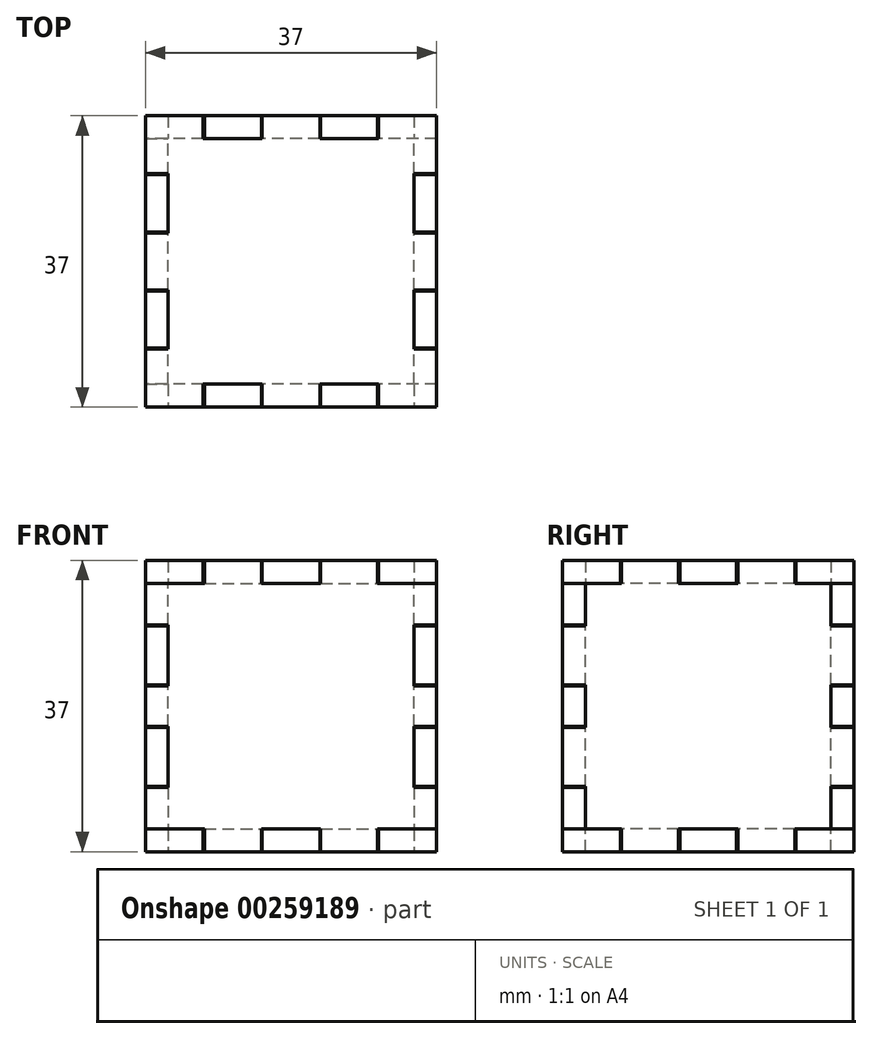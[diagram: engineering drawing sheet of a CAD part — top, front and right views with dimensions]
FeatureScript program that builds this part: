
annotation { "Feature Type Name" : "Feature", "Feature Type Description" : "" }
export const myFeature = defineFeature(function(context is Context, id is Id, definition is map)
    precondition{}
    {
        {
            assignVariable(context, id + "F0", {"name" : "Edge", "anyValue" : 37 * mm});
        }
        {
            assignVariable(context, id + "F1", {"name" : "T", "anyValue" : 2.9 * mm});
        }
        {
            var Q0;
            Q0=qCreatedBy(makeId("Top.planeOp"),FACE);
            var sketch = newSketch(context, id + "F2", { "sketchPlane" : qUnion([Q0])});
            skLineSegment(sketch, "E0.bottom", {"start": v(0, 0) * mm, "end": v(7.5, 0) * mm});
            skLineSegment(sketch, "E0.top", {"start": v(0, 37) * mm, "end": v(7.5, 37) * mm});
            skLineSegment(sketch, "E0.left", {"start": v(0, 0) * mm, "end": v(0, 7.5) * mm});
            skLineSegment(sketch, "E0.right", {"start": v(37, 0) * mm, "end": v(37, 7.5) * mm});
            skLineSegment(sketch, "E1", {"start": v(14.75, 37) * mm, "end": v(14.75, 34.1) * mm});
            skLineSegment(sketch, "E2", {"start": v(7.5, 34.1) * mm, "end": v(14.75, 34.1) * mm});
            skLineSegment(sketch, "E3", {"start": v(7.5, 34.1) * mm, "end": v(7.5, 37) * mm});
            skLineSegment(sketch, "E4.trimOffspring", {"start": v(14.75, 37) * mm, "end": v(22.25, 37) * mm});
            skLineSegment(sketch, "E5", {"start": v(22.25, 37) * mm, "end": v(22.25, 34.1) * mm});
            skLineSegment(sketch, "E6", {"start": v(22.25, 34.1) * mm, "end": v(29.5, 34.1) * mm});
            skLineSegment(sketch, "E7", {"start": v(29.5, 34.1) * mm, "end": v(29.5, 37) * mm});
            skLineSegment(sketch, "E8.trimOffspring", {"start": v(29.5, 37) * mm, "end": v(37, 37) * mm});
            skLineSegment(sketch, "E9", {"start": v(0, 29.5) * mm, "end": v(2.89, 29.5) * mm});
            skLineSegment(sketch, "E10", {"start": v(2.89, 29.5) * mm, "end": v(2.89, 22.25) * mm});
            skLineSegment(sketch, "E11", {"start": v(2.9, 22.25) * mm, "end": v(0, 22.25) * mm});
            skLineSegment(sketch, "E12.trimOffspring", {"start": v(0, 29.5) * mm, "end": v(0, 37) * mm});
            skLineSegment(sketch, "E13", {"start": v(0, 14.75) * mm, "end": v(2.9, 14.75) * mm});
            skLineSegment(sketch, "E14", {"start": v(2.9, 14.75) * mm, "end": v(2.9, 7.5) * mm});
            skLineSegment(sketch, "E15", {"start": v(2.89, 7.5) * mm, "end": v(0, 7.5) * mm});
            skLineSegment(sketch, "E16.trimOffspring", {"start": v(0, 14.75) * mm, "end": v(0, 22.25) * mm});
            skLineSegment(sketch, "E17", {"start": v(7.5, 0) * mm, "end": v(7.5, 2.89) * mm});
            skLineSegment(sketch, "E18", {"start": v(7.5, 2.89) * mm, "end": v(14.75, 2.89) * mm});
            skLineSegment(sketch, "E19", {"start": v(14.75, 2.9) * mm, "end": v(14.75, 0) * mm});
            skLineSegment(sketch, "E20", {"start": v(14.75, 0) * mm, "end": v(22.25, 0) * mm});
            skLineSegment(sketch, "E21", {"start": v(22.25, 0) * mm, "end": v(22.25, 2.9) * mm});
            skLineSegment(sketch, "E22", {"start": v(22.25, 2.89) * mm, "end": v(29.5, 2.89) * mm});
            skLineSegment(sketch, "E23", {"start": v(29.5, 2.9) * mm, "end": v(29.5, 0) * mm});
            skLineSegment(sketch, "E24.trimOffspring", {"start": v(29.5, 0) * mm, "end": v(37, 0) * mm});
            skLineSegment(sketch, "E25", {"start": v(37, 14.75) * mm, "end": v(37, 22.25) * mm});
            skLineSegment(sketch, "E26.trimOffspring", {"start": v(37, 29.5) * mm, "end": v(37, 37) * mm});
            skLineSegment(sketch, "E27", {"start": v(37, 29.5) * mm, "end": v(34.11, 29.5) * mm});
            skLineSegment(sketch, "E28", {"start": v(34.11, 22.25) * mm, "end": v(34.11, 29.5) * mm});
            skLineSegment(sketch, "E29", {"start": v(34.11, 22.25) * mm, "end": v(37, 22.25) * mm});
            skLineSegment(sketch, "E30", {"start": v(37, 14.75) * mm, "end": v(34.11, 14.75) * mm});
            skLineSegment(sketch, "E31", {"start": v(34.11, 14.75) * mm, "end": v(34.11, 7.5) * mm});
            skLineSegment(sketch, "E32", {"start": v(37, 7.5) * mm, "end": v(34.11, 7.5) * mm});
            skSolve(sketch);
        }
        {
            var Q0;
            Q0=makeQuery(id+"F2.imprint","IMPRINT",FACE,{"disambiguationData":[TD([[makeQuery(id+"F2.imprint","IMPRINT",EDGE,{"derivedFrom":sQuery(id+"F2.wireOp",EDGE,"E0.bottom")}),1.0]])]});
            extrude(context, id + "F3", {"entities" : qUnion([Q0]), "depth" : getVariable(context, 'T')});
        }
        {
            var Q0;
            Q0=makeQuery(id+"F2.imprint","IMPRINT",FACE,{"disambiguationData":[TD([[makeQuery(id+"F2.imprint","IMPRINT",EDGE,{"derivedFrom":sQuery(id+"F2.wireOp",EDGE,"E0.bottom")}),1.0]])]});
            extrude(context, id + "F4", {"entities" : qUnion([Q0]), "depth" : getVariable(context, 'Edge'), "hasSecondDirection" : true, "secondDirectionOppositeDirection" : false, "secondDirectionDepth" : getVariable(context, 'Edge') - getVariable(context, 'T')});
        }
        {
            var Q0;
            Q0=qCreatedBy(makeId("Front.planeOp"),FACE);
            var sketch = newSketch(context, id + "F5", { "sketchPlane" : qUnion([Q0])});
            skLineSegment(sketch, "E33.top", {"start": v(7.36, 37) * mm, "end": v(14.82, 37) * mm});
            skLineSegment(sketch, "E33.left", {"start": v(0, 2.9) * mm, "end": v(0, 8.3) * mm});
            skLineSegment(sketch, "E34", {"start": v(37, 2.9) * mm, "end": v(29.64, 2.9) * mm});
            skLineSegment(sketch, "E35", {"start": v(29.64, 2.9) * mm, "end": v(29.64, 0) * mm});
            skLineSegment(sketch, "E36", {"start": v(22.18, 0) * mm, "end": v(22.18, 2.9) * mm});
            skLineSegment(sketch, "E37", {"start": v(22.18, 2.9) * mm, "end": v(14.82, 2.9) * mm});
            skLineSegment(sketch, "E38", {"start": v(14.82, 2.9) * mm, "end": v(14.82, 0) * mm});
            skLineSegment(sketch, "E39.trimOffspring", {"start": v(22.18, 0) * mm, "end": v(29.64, 0) * mm});
            skLineSegment(sketch, "E40", {"start": v(0, 2.89) * mm, "end": v(0, 2.89) * mm});
            skLineSegment(sketch, "E41", {"start": v(37, 2.9) * mm, "end": v(37, 2.9) * mm});
            skLineSegment(sketch, "E42", {"start": v(37, 2.9) * mm, "end": v(37, 8.3) * mm});
            skLineSegment(sketch, "E43", {"start": v(0, 8.3) * mm, "end": v(2.89, 8.3) * mm});
            skLineSegment(sketch, "E44", {"start": v(2.89, 8.3) * mm, "end": v(2.89, 15.8) * mm});
            skLineSegment(sketch, "E45", {"start": v(2.89, 15.8) * mm, "end": v(0, 15.8) * mm});
            skLineSegment(sketch, "E46", {"start": v(0, 21.2) * mm, "end": v(2.89, 21.2) * mm});
            skLineSegment(sketch, "E47", {"start": v(2.89, 21.2) * mm, "end": v(2.89, 28.7) * mm});
            skLineSegment(sketch, "E48", {"start": v(0, 28.7) * mm, "end": v(2.89, 28.7) * mm});
            skLineSegment(sketch, "E49.trimOffspring", {"start": v(0, 28.7) * mm, "end": v(0, 34.1) * mm});
            skLineSegment(sketch, "E50.trimOffspring", {"start": v(0, 15.8) * mm, "end": v(0, 21.2) * mm});
            skLineSegment(sketch, "E51", {"start": v(0, 34.1) * mm, "end": v(7.36, 34.1) * mm});
            skLineSegment(sketch, "E52", {"start": v(7.36, 37) * mm, "end": v(7.36, 34.1) * mm});
            skLineSegment(sketch, "E53", {"start": v(14.82, 37) * mm, "end": v(14.82, 34.1) * mm});
            skLineSegment(sketch, "E54", {"start": v(14.82, 34.1) * mm, "end": v(22.18, 34.1) * mm});
            skLineSegment(sketch, "E55", {"start": v(22.18, 37) * mm, "end": v(22.18, 34.1) * mm});
            skLineSegment(sketch, "E56", {"start": v(37, 34.1) * mm, "end": v(29.64, 34.1) * mm});
            skLineSegment(sketch, "E57", {"start": v(29.64, 37) * mm, "end": v(29.64, 34.1) * mm});
            skLineSegment(sketch, "E58.trimOffspring", {"start": v(22.18, 37) * mm, "end": v(29.64, 37) * mm});
            skLineSegment(sketch, "E59", {"start": v(37, 28.7) * mm, "end": v(34.1, 28.7) * mm});
            skLineSegment(sketch, "E60", {"start": v(34.1, 21.2) * mm, "end": v(34.1, 28.7) * mm});
            skLineSegment(sketch, "E61", {"start": v(34.1, 21.2) * mm, "end": v(37, 21.2) * mm});
            skLineSegment(sketch, "E62", {"start": v(37, 15.8) * mm, "end": v(34.1, 15.8) * mm});
            skLineSegment(sketch, "E63", {"start": v(34.1, 15.8) * mm, "end": v(34.1, 8.3) * mm});
            skLineSegment(sketch, "E64", {"start": v(37, 8.3) * mm, "end": v(34.1, 8.3) * mm});
            skLineSegment(sketch, "E65.trimOffspring", {"start": v(37, 15.8) * mm, "end": v(37, 21.2) * mm});
            skLineSegment(sketch, "E66.trimOffspring", {"start": v(37, 28.7) * mm, "end": v(37, 34.1) * mm});
            skLineSegment(sketch, "E67", {"start": v(7.36, 0) * mm, "end": v(7.36, 2.9) * mm});
            skLineSegment(sketch, "E68", {"start": v(7.36, 2.9) * mm, "end": v(0, 2.89) * mm});
            skLineSegment(sketch, "E69", {"start": v(7.36, 0) * mm, "end": v(14.82, 0) * mm});
            skPoint(sketch, "E70.start.orphan", {"position": v(0, 2.89) * mm});
            skSolve(sketch);
        }
        {
            var Q0;
            Q0=makeQuery(id+"F5.imprint","IMPRINT",FACE,{"disambiguationData":[TD([[makeQuery(id+"F5.imprint","IMPRINT",EDGE,{"derivedFrom":sQuery(id+"F5.wireOp",EDGE,"E33.top")}),-1.0]])]});
            extrude(context, id + "F6", {"entities" : qUnion([Q0]), "oppositeDirection" : true, "depth" : getVariable(context, 'T')});
        }
        {
            var Q0;
            Q0=makeQuery(id+"F5.imprint","IMPRINT",FACE,{"disambiguationData":[TD([[makeQuery(id+"F5.imprint","IMPRINT",EDGE,{"derivedFrom":sQuery(id+"F5.wireOp",EDGE,"E33.top")}),-1.0]])]});
            extrude(context, id + "F7", {"entities" : qUnion([Q0]), "oppositeDirection" : true, "depth" : getVariable(context, 'Edge'), "hasSecondDirection" : true, "secondDirectionOppositeDirection" : true, "secondDirectionDepth" : getVariable(context, 'Edge') - getVariable(context, 'T')});
        }
        {
            var Q0;
            Q0=qCreatedBy(makeId("Right.planeOp"),FACE);
            var sketch = newSketch(context, id + "F8", { "sketchPlane" : qUnion([Q0])});
            skLineSegment(sketch, "E71.bottom", {"start": v(29.64, 37) * mm, "end": v(22.1, 37) * mm});
            skLineSegment(sketch, "E71.top", {"start": v(29.64, 0) * mm, "end": v(22.1, 0) * mm});
            skLineSegment(sketch, "E71.left", {"start": v(37, 28.84) * mm, "end": v(37, 21.06) * mm});
            skLineSegment(sketch, "E72", {"start": v(0, 8.16) * mm, "end": v(2.89, 8.16) * mm});
            skLineSegment(sketch, "E73", {"start": v(2.89, 8.16) * mm, "end": v(2.9, 2.89) * mm});
            skLineSegment(sketch, "E74", {"start": v(2.9, 2.89) * mm, "end": v(7.36, 2.9) * mm});
            skLineSegment(sketch, "E75", {"start": v(7.36, 2.9) * mm, "end": v(7.36, 0) * mm});
            skLineSegment(sketch, "E76", {"start": v(14.9, 2.89) * mm, "end": v(22.1, 2.9) * mm});
            skLineSegment(sketch, "E77", {"start": v(22.1, 0) * mm, "end": v(22.1, 2.9) * mm});
            skLineSegment(sketch, "E78.trimOffspring", {"start": v(14.9, 0) * mm, "end": v(7.36, 0) * mm});
            skLineSegment(sketch, "E79", {"start": v(29.64, 0) * mm, "end": v(29.64, 2.89) * mm});
            skLineSegment(sketch, "E80", {"start": v(29.64, 2.89) * mm, "end": v(34.1, 2.9) * mm});
            skLineSegment(sketch, "E81", {"start": v(0, 15.94) * mm, "end": v(2.89, 15.94) * mm});
            skLineSegment(sketch, "E82", {"start": v(2.89, 15.94) * mm, "end": v(2.89, 21.06) * mm});
            skLineSegment(sketch, "E83", {"start": v(0, 21.06) * mm, "end": v(2.89, 21.06) * mm});
            skLineSegment(sketch, "E84.trimOffspring", {"start": v(0, 15.94) * mm, "end": v(0, 8.16) * mm});
            skLineSegment(sketch, "E85", {"start": v(0, 28.84) * mm, "end": v(2.89, 28.84) * mm});
            skLineSegment(sketch, "E86", {"start": v(2.89, 28.84) * mm, "end": v(2.89, 34.1) * mm});
            skLineSegment(sketch, "E87.trimOffspring", {"start": v(0, 28.84) * mm, "end": v(0, 21.06) * mm});
            skPoint(sketch, "E88.orphan", {"position": v(0, 37) * mm});
            skLineSegment(sketch, "E89", {"start": v(2.89, 34.1) * mm, "end": v(7.36, 34.1) * mm});
            skLineSegment(sketch, "E90", {"start": v(7.36, 37) * mm, "end": v(7.36, 34.1) * mm});
            skLineSegment(sketch, "E91", {"start": v(14.89, 37) * mm, "end": v(14.89, 34.1) * mm});
            skLineSegment(sketch, "E92", {"start": v(22.1, 34.1) * mm, "end": v(14.89, 34.1) * mm});
            skLineSegment(sketch, "E93", {"start": v(22.1, 34.1) * mm, "end": v(22.1, 37) * mm});
            skLineSegment(sketch, "E94.trimOffspring", {"start": v(14.89, 37) * mm, "end": v(7.36, 37) * mm});
            skLineSegment(sketch, "E95", {"start": v(29.64, 37) * mm, "end": v(29.64, 34.11) * mm});
            skLineSegment(sketch, "E96", {"start": v(34.1, 34.1) * mm, "end": v(29.64, 34.1) * mm});
            skLineSegment(sketch, "E97", {"start": v(34.1, 34.11) * mm, "end": v(34.1, 28.84) * mm});
            skLineSegment(sketch, "E98", {"start": v(37, 28.84) * mm, "end": v(34.1, 28.84) * mm});
            skLineSegment(sketch, "E99", {"start": v(37, 21.06) * mm, "end": v(34.1, 21.06) * mm});
            skLineSegment(sketch, "E100", {"start": v(34.1, 21.06) * mm, "end": v(34.1, 15.94) * mm});
            skLineSegment(sketch, "E101", {"start": v(37, 15.94) * mm, "end": v(34.1, 15.94) * mm});
            skLineSegment(sketch, "E102.trimOffspring", {"start": v(37, 15.94) * mm, "end": v(37, 8.16) * mm});
            skLineSegment(sketch, "E103", {"start": v(37, 8.16) * mm, "end": v(34.1, 8.16) * mm});
            skLineSegment(sketch, "E104", {"start": v(34.1, 2.9) * mm, "end": v(34.1, 8.16) * mm});
            skLineSegment(sketch, "E105", {"start": v(14.9, 2.89) * mm, "end": v(14.9, 0) * mm});
            skSolve(sketch);
        }
        {
            var Q0;
            Q0=makeQuery(id+"F8.imprint","IMPRINT",FACE,{"disambiguationData":[TD([[makeQuery(id+"F8.imprint","IMPRINT",EDGE,{"derivedFrom":sQuery(id+"F8.wireOp",EDGE,"E71.bottom")}),1.0]])]});
            extrude(context, id + "F9", {"entities" : qUnion([Q0]), "depth" : getVariable(context, 'T')});
        }
        {
            var Q0;
            Q0=makeQuery(id+"F8.imprint","IMPRINT",FACE,{"disambiguationData":[TD([[makeQuery(id+"F8.imprint","IMPRINT",EDGE,{"derivedFrom":sQuery(id+"F8.wireOp",EDGE,"E71.bottom")}),1.0]])]});
            extrude(context, id + "F10", {"entities" : qUnion([Q0]), "depth" : getVariable(context, 'Edge'), "hasSecondDirection" : true, "secondDirectionOppositeDirection" : false, "secondDirectionDepth" : getVariable(context, 'Edge') - getVariable(context, 'T')});
        }
    });
